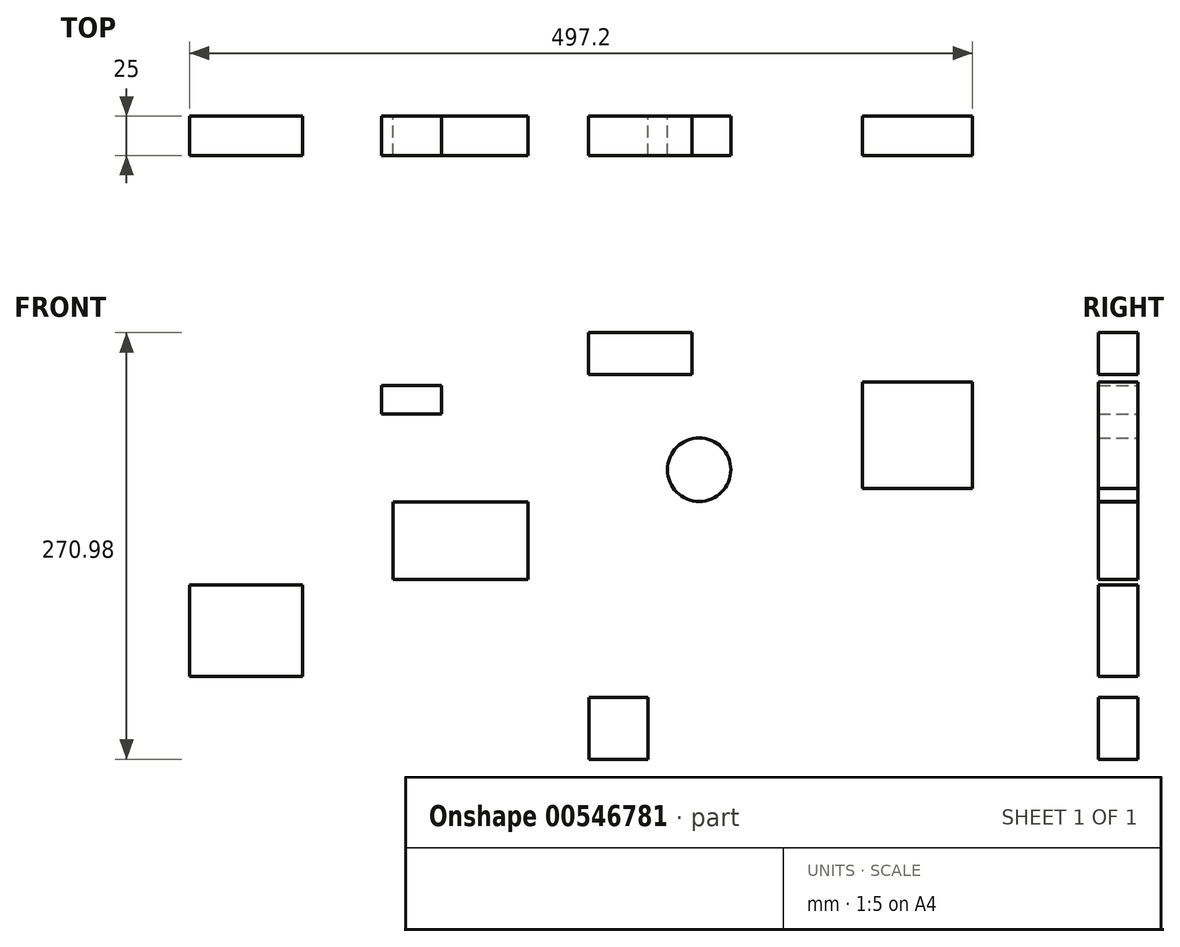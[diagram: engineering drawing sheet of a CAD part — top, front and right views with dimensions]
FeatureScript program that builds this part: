
annotation { "Feature Type Name" : "Feature", "Feature Type Description" : "" }
export const myFeature = defineFeature(function(context is Context, id is Id, definition is map)
    precondition{}
    {
        {
            var Q0;
            Q0=qCreatedBy(makeId("Front.planeOp"),FACE);
            var sketch = newSketch(context, id + "F0", { "sketchPlane" : qUnion([Q0])});
            skLineSegment(sketch, "E0.bottom", {"start": v(-85.78, 13.29) * mm, "end": v(0, 13.29) * mm});
            skLineSegment(sketch, "E0.top", {"start": v(-85.78, -35.96) * mm, "end": v(0, -35.96) * mm});
            skLineSegment(sketch, "E0.left", {"start": v(-85.78, 13.29) * mm, "end": v(-85.78, -35.96) * mm});
            skLineSegment(sketch, "E0.right", {"start": v(0, 13.29) * mm, "end": v(0, -35.96) * mm});
            skSolve(sketch);
        }
        {
            var Q0;
            Q0 = qSketchRegion(id + "F0", true);
            extrude(context, id + "F1", {"entities" : qUnion([Q0]), "depth" : 25 * mm, "offsetDistance" : 25 * mm});
        }
        {
            var Q0;
            Q0=qCreatedBy(makeId("Front.planeOp"),FACE);
            var sketch = newSketch(context, id + "F2", { "sketchPlane" : qUnion([Q0])});
            skCircle(sketch, "E1", {"center": v(108.65, 33.67) * mm, "radius": 20.15 * mm});
            skLineSegment(sketch, "E2.bottom", {"start": v(-92.99, 87.28) * mm, "end": v(-55.12, 87.28) * mm});
            skLineSegment(sketch, "E2.top", {"start": v(-92.99, 69.08) * mm, "end": v(-55.12, 69.08) * mm});
            skLineSegment(sketch, "E2.left", {"start": v(-92.99, 87.28) * mm, "end": v(-92.99, 69.08) * mm});
            skLineSegment(sketch, "E2.right", {"start": v(-55.12, 87.28) * mm, "end": v(-55.12, 69.08) * mm});
            skLineSegment(sketch, "E3.bottom", {"start": v(38.32, 120.72) * mm, "end": v(104.22, 120.72) * mm});
            skLineSegment(sketch, "E3.top", {"start": v(38.32, 94.16) * mm, "end": v(104.22, 94.16) * mm});
            skLineSegment(sketch, "E3.left", {"start": v(38.32, 120.72) * mm, "end": v(38.32, 94.16) * mm});
            skLineSegment(sketch, "E3.right", {"start": v(104.22, 120.72) * mm, "end": v(104.22, 94.16) * mm});
            skLineSegment(sketch, "E4.bottom", {"start": v(212.42, 89.25) * mm, "end": v(282.25, 89.25) * mm});
            skLineSegment(sketch, "E4.top", {"start": v(212.42, 21.87) * mm, "end": v(282.25, 21.87) * mm});
            skLineSegment(sketch, "E4.left", {"start": v(212.42, 89.25) * mm, "end": v(212.42, 21.87) * mm});
            skLineSegment(sketch, "E4.right", {"start": v(282.25, 89.25) * mm, "end": v(282.25, 21.87) * mm});
            skLineSegment(sketch, "E5.bottom", {"start": v(38.82, -110.91) * mm, "end": v(76.2, -110.91) * mm});
            skLineSegment(sketch, "E5.top", {"start": v(38.82, -150.26) * mm, "end": v(76.2, -150.26) * mm});
            skLineSegment(sketch, "E5.left", {"start": v(38.82, -110.91) * mm, "end": v(38.82, -150.26) * mm});
            skLineSegment(sketch, "E5.right", {"start": v(76.2, -110.91) * mm, "end": v(76.2, -150.26) * mm});
            skLineSegment(sketch, "E6.bottom", {"start": v(-214.95, -39.6) * mm, "end": v(-143.15, -39.6) * mm});
            skLineSegment(sketch, "E6.top", {"start": v(-214.95, -97.63) * mm, "end": v(-143.15, -97.63) * mm});
            skLineSegment(sketch, "E6.left", {"start": v(-214.95, -39.6) * mm, "end": v(-214.95, -97.63) * mm});
            skLineSegment(sketch, "E6.right", {"start": v(-143.15, -39.6) * mm, "end": v(-143.15, -97.63) * mm});
            skSolve(sketch);
        }
        {
            var Q0;
            Q0 = qSketchRegion(id + "F2", true);
            extrude(context, id + "F3", {"entities" : qUnion([Q0]), "depth" : 25 * mm, "offsetDistance" : 25 * mm});
        }
    });
